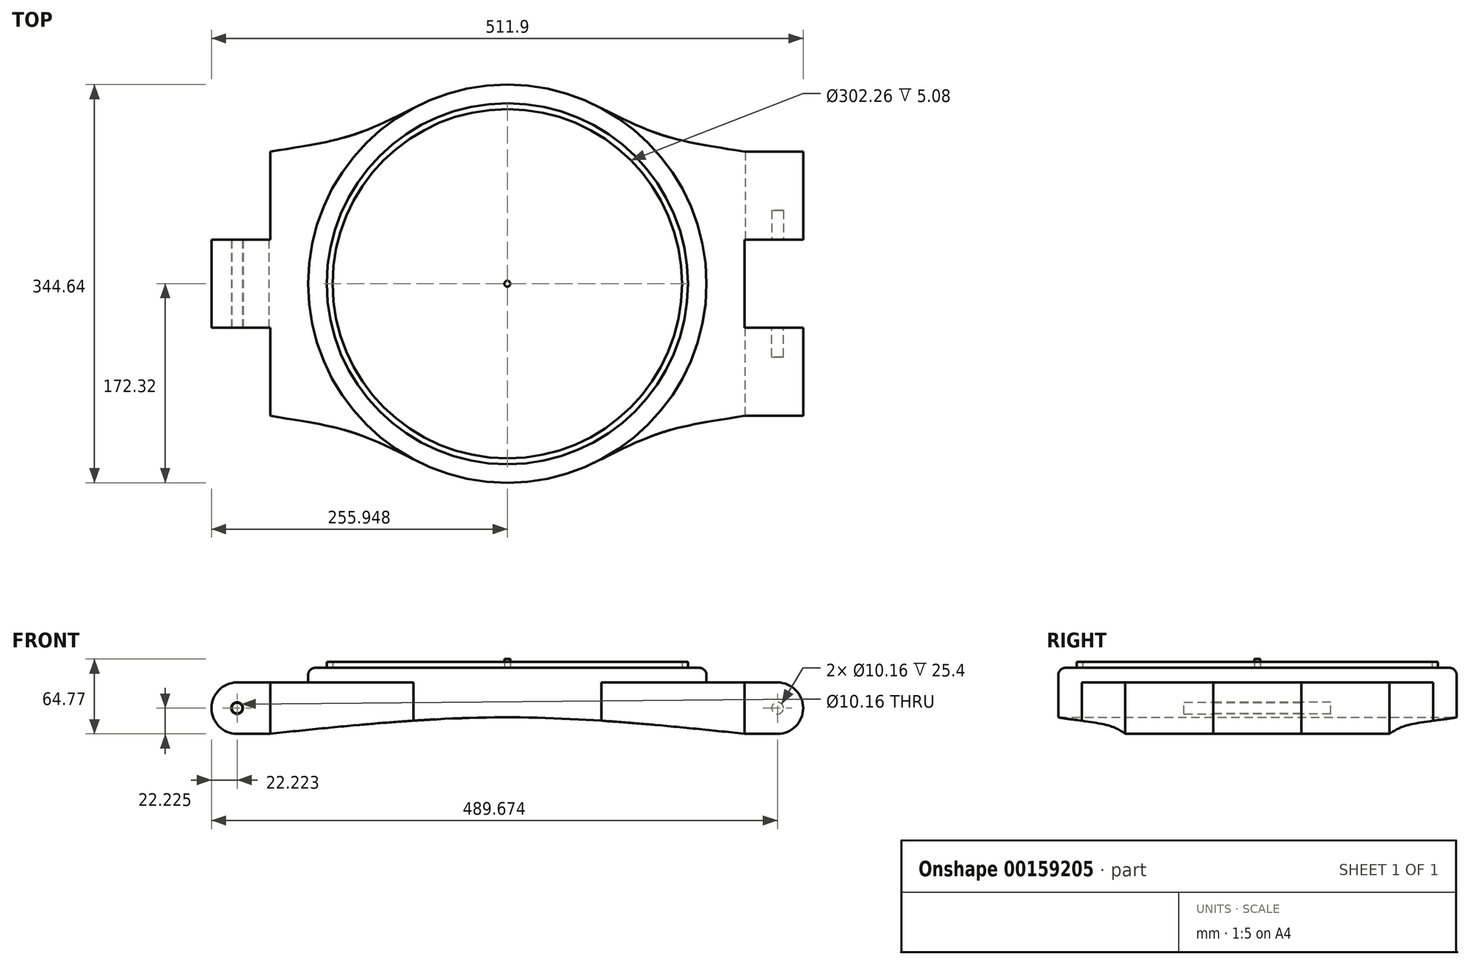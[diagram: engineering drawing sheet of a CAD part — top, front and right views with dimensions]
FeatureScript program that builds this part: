
annotation { "Feature Type Name" : "Feature", "Feature Type Description" : "" }
export const myFeature = defineFeature(function(context is Context, id is Id, definition is map)
    precondition{}
    {
        {
            var Q0;
            Q0=qCreatedBy(makeId("Top.planeOp"),FACE);
            var sketch = newSketch(context, id + "F0", { "sketchPlane" : qUnion([Q0])});
            skLineSegment(sketch, "E0", {"start": v(-15.4, -76.2) * mm, "end": v(-91.6, -76.2) * mm});
            skLineSegment(sketch, "E1", {"start": v(-91.6, -76.2) * mm, "end": v(-91.6, 0) * mm});
            skLineSegment(sketch, "E2", {"start": v(-91.6, 0) * mm, "end": v(-142.4, 0) * mm});
            skLineSegment(sketch, "E3", {"start": v(-142.4, 0) * mm, "end": v(-142.4, 76.2) * mm});
            skLineSegment(sketch, "E4", {"start": v(-142.4, 76.2) * mm, "end": v(-91.6, 76.2) * mm});
            skLineSegment(sketch, "E5", {"start": v(-91.6, 76.2) * mm, "end": v(-91.6, 152.4) * mm});
            skLineSegment(sketch, "E6", {"start": v(-91.6, 152.4) * mm, "end": v(-15.4, 152.4) * mm});
            skLineSegment(sketch, "E7", {"start": v(-15.4, 152.4) * mm, "end": v(-15.4, -76.2) * mm});
            skCircle(sketch, "E8", {"center": v(113.55, 38.1) * mm, "radius": 172.32 * mm});
            skPoint(sketch, "E8.centerSnap0", {"position": v(-15.4, 38.1) * mm});
            skLineSegment(sketch, "E9", {"start": v(242.5, 152.4) * mm, "end": v(242.5, -76.2) * mm});
            skLineSegment(sketch, "E10", {"start": v(242.5, -76.2) * mm, "end": v(369.5, -76.2) * mm});
            skLineSegment(sketch, "E11", {"start": v(369.5, -76.2) * mm, "end": v(369.5, 0) * mm});
            skLineSegment(sketch, "E12", {"start": v(369.5, 0) * mm, "end": v(318.7, 0) * mm});
            skLineSegment(sketch, "E13", {"start": v(318.7, 0) * mm, "end": v(318.7, 76.2) * mm});
            skLineSegment(sketch, "E14", {"start": v(318.7, 76.2) * mm, "end": v(369.5, 76.2) * mm});
            skLineSegment(sketch, "E15", {"start": v(369.5, 76.2) * mm, "end": v(369.5, 152.4) * mm});
            skLineSegment(sketch, "E16", {"start": v(369.5, 152.4) * mm, "end": v(242.5, 152.4) * mm});
            skFitSpline(sketch, "E17", {"points": [v(-91.6, -76.2) * mm, v(32.25, -113.83) * mm], "startDerivative": vector(178.39, -29.4) * mm, "endDerivative": vector(159.39, -81.53) * mm});
            skFitSpline(sketch, "E18.MirrorCS", {"points": [v(318.7, -76.2) * mm, v(194.84, -113.83) * mm], "startDerivative": vector(-178.39, -29.4) * mm, "endDerivative": vector(-159.39, -81.53) * mm});
            skFitSpline(sketch, "E19.MirrorCS", {"points": [v(318.7, 152.4) * mm, v(194.84, 190.03) * mm], "startDerivative": vector(-178.39, 29.4) * mm, "endDerivative": vector(-159.39, 81.53) * mm});
            skFitSpline(sketch, "E20.MirrorCS", {"points": [v(-91.6, 152.4) * mm, v(32.25, 190.03) * mm], "startDerivative": vector(178.39, 29.4) * mm, "endDerivative": vector(159.39, 81.53) * mm});
            skSolve(sketch);
        }
        {
            var Q0;
            {var subQ1=sQuery(id+"F0.wireOp",EDGE,"E7");Q0=makeQuery(id+"F0.imprint","IMPRINT",FACE,{"disambiguationData":[TD([[makeQuery(id+"F0.imprint","IMPRINT",EDGE,{"derivedFrom":subQ1}),1.0]])]});}
            var Q1;
            {var subQ0=sQuery(id+"F0.wireOp",EDGE,"E6");Q1=makeQuery(id+"F0.imprint","IMPRINT",FACE,{"disambiguationData":[TD([[makeQuery(id+"F0.imprint","IMPRINT",EDGE,{"derivedFrom":subQ0}),1.0]])]});}
            var Q2;
            {var subQ0=sQuery(id+"F0.wireOp",EDGE,"E0");Q2=makeQuery(id+"F0.imprint","IMPRINT",FACE,{"disambiguationData":[TD([[makeQuery(id+"F0.imprint","IMPRINT",EDGE,{"derivedFrom":subQ0}),-1.0]])]});}
            var Q3;
            {var subQ0=sQuery(id+"F0.wireOp",EDGE,"E0");Q3=makeQuery(id+"F0.imprint","IMPRINT",FACE,{"disambiguationData":[TD([[makeQuery(id+"F0.imprint","IMPRINT",EDGE,{"derivedFrom":subQ0}),1.0]])]});}
            var Q4;
            {var subQ0=sQuery(id+"F0.wireOp",EDGE,"E7");Q4=makeQuery(id+"F0.imprint","IMPRINT",FACE,{"disambiguationData":[TD([[makeQuery(id+"F0.imprint","IMPRINT",EDGE,{"derivedFrom":subQ0}),-1.0]])]});}
            var Q5;
            {var subQ0=sQuery(id+"F0.wireOp",EDGE,"E9");Q5=makeQuery(id+"F0.imprint","IMPRINT",FACE,{"disambiguationData":[TD([[makeQuery(id+"F0.imprint","IMPRINT",EDGE,{"derivedFrom":subQ0}),1.0]])]});}
            var Q6;
            {var subQ3=sQuery(id+"F0.wireOp",EDGE,"E18.MirrorCS");Q6=makeQuery(id+"F0.imprint","IMPRINT",FACE,{"disambiguationData":[TD([[makeQuery(id+"F0.imprint","IMPRINT",EDGE,{"derivedFrom":subQ3}),-1.0]])]});}
            var Q7;
            {var subQ0=sQuery(id+"F0.wireOp",EDGE,"E11");Q7=makeQuery(id+"F0.imprint","IMPRINT",FACE,{"disambiguationData":[TD([[makeQuery(id+"F0.imprint","IMPRINT",EDGE,{"derivedFrom":subQ0}),1.0]])]});}
            var Q8;
            {var subQ3=sQuery(id+"F0.wireOp",EDGE,"E19.MirrorCS");Q8=makeQuery(id+"F0.imprint","IMPRINT",FACE,{"disambiguationData":[TD([[makeQuery(id+"F0.imprint","IMPRINT",EDGE,{"derivedFrom":subQ3}),1.0]])]});}
            extrude(context, id + "F1", {"entities" : qUnion([Q0, Q1, Q2, Q3, Q4, Q5, Q6, Q7, Q8]), "oppositeDirection" : true, "depth" : 44.45 * mm});
        }
        {
            var Q0;
            Q0=makeQuery(id+"F1.opExtrude","CAP_EDGE",EDGE,{"disambiguationData":[OSD([sQuery(id+"F0.wireOp",EDGE,"E3")])],"isStart":true});
            var Q1;
            Q1=makeQuery(id+"F1.opExtrude","CAP_EDGE",EDGE,{"disambiguationData":[OSD([sQuery(id+"F0.wireOp",EDGE,"E3")])],"isStart":false});
            var Q2;
            Q2=makeQuery(id+"F1.opExtrude","CAP_EDGE",EDGE,{"disambiguationData":[OSD([sQuery(id+"F0.wireOp",EDGE,"E11")])],"isStart":true});
            var Q3;
            Q3=makeQuery(id+"F1.opExtrude","CAP_EDGE",EDGE,{"disambiguationData":[OSD([sQuery(id+"F0.wireOp",EDGE,"E15")])],"isStart":true});
            var Q4;
            Q4=makeQuery(id+"F1.opExtrude","CAP_EDGE",EDGE,{"disambiguationData":[OSD([sQuery(id+"F0.wireOp",EDGE,"E15")])],"isStart":false});
            var Q5;
            Q5=makeQuery(id+"F1.opExtrude","CAP_EDGE",EDGE,{"disambiguationData":[OSD([sQuery(id+"F0.wireOp",EDGE,"E11")])],"isStart":false});
            fillet(context, id + "F2", {"entities" : qUnion([Q0, Q1, Q2, Q3, Q4, Q5]), "radius" : 22.22 * mm, "tangentPropagation" : true, "allowEdgeOverflow" : false});
        }
        {
            var Q0;
            {var subQ1=sQuery(id+"F0.wireOp",EDGE,"E7");Q0=makeQuery(id+"F0.imprint","IMPRINT",FACE,{"disambiguationData":[TD([[makeQuery(id+"F0.imprint","IMPRINT",EDGE,{"derivedFrom":subQ1}),1.0]])]});}
            var Q1;
            {var subQ0=sQuery(id+"F0.wireOp",EDGE,"E7");Q1=makeQuery(id+"F0.imprint","IMPRINT",FACE,{"disambiguationData":[TD([[makeQuery(id+"F0.imprint","IMPRINT",EDGE,{"derivedFrom":subQ0}),-1.0]])]});}
            var Q2;
            {var subQ0=sQuery(id+"F0.wireOp",EDGE,"E9");Q2=makeQuery(id+"F0.imprint","IMPRINT",FACE,{"disambiguationData":[TD([[makeQuery(id+"F0.imprint","IMPRINT",EDGE,{"derivedFrom":subQ0}),1.0]])]});}
            extrude(context, id + "F3", {"entities" : qUnion([Q0, Q1, Q2]), "operationType" : NewBodyOperationType.ADD, "depth" : 12.7 * mm});
        }
        {
            var Q0;
            Q0=qCreatedBy(makeId("Front.planeOp"),FACE);
            var sketch = newSketch(context, id + "F4", { "sketchPlane" : qUnion([Q0])});
            skFitSpline(sketch, "E21", {"points": [v(-92.66, -44.45) * mm, v(113.22, -30.2) * mm, v(319.28, -44.45) * mm], "startDerivative": vector(411.8, 42.76) * mm, "endDerivative": vector(412.09, -42.76) * mm});
            skLineSegment(sketch, "E22", {"start": v(-92.66, -44.45) * mm, "end": v(319.28, -44.45) * mm});
            skSolve(sketch);
        }
        {
            var Q0;
            Q0 = qSketchRegion(id + "F4", true);
            extrude(context, id + "F5", {"entities" : qUnion([Q0]), "operationType" : NewBodyOperationType.REMOVE, "endBound" : BoundingType.THROUGH_ALL, "oppositeDirection" : true, "depth" : 254 * mm});
        }
        {
            var Q0;
            Q0 = qSketchRegion(id + "F4", true);
            extrude(context, id + "F6", {"entities" : qUnion([Q0]), "operationType" : NewBodyOperationType.REMOVE, "endBound" : BoundingType.THROUGH_ALL, "depth" : 25.4 * mm});
        }
        {
            var Q0;
            Q0=qCreatedBy(makeId("Front.planeOp"),FACE);
            var sketch = newSketch(context, id + "F7", { "sketchPlane" : qUnion([Q0])});
            skCircle(sketch, "E23", {"center": v(-120.18, -22.23) * mm, "radius": 5.08 * mm});
            skCircle(sketch, "E24", {"center": v(-120.18, -22.23) * mm, "radius": 4.6 * mm});
            skCircle(sketch, "E25", {"center": v(347.27, -22.23) * mm, "radius": 5.08 * mm});
            skSolve(sketch);
        }
        {
            var Q0;
            Q0 = qSketchRegion(id + "F7", true);
            extrude(context, id + "F8", {"entities" : qUnion([Q0]), "operationType" : NewBodyOperationType.REMOVE, "oppositeDirection" : true, "depth" : 101.6 * mm});
        }
        {
            var Q0;
            Q0 = qSketchRegion(id + "F7", true);
            extrude(context, id + "F9", {"entities" : qUnion([Q0]), "operationType" : NewBodyOperationType.REMOVE, "depth" : 25.4 * mm});
        }
        {
            var Q0;
            Q0=makeQuery(id+"F3.opExtrude","CAP_EDGE",EDGE,{"disambiguationData":[OSD([sQuery(id+"F0.wireOp",EDGE,"E8")])],"isStart":false});
            fillet(context, id + "F10", {"entities" : qUnion([Q0]), "radius" : 6.35 * mm, "tangentPropagation" : true, "allowEdgeOverflow" : false});
        }
        {
            var Q0;
            Q0=qCreatedBy(makeId("Top.planeOp"),FACE);
            var sketch = newSketch(context, id + "F11", { "sketchPlane" : qUnion([Q0])});
            skCircle(sketch, "E26", {"center": v(113.55, 38.1) * mm, "radius": 156.21 * mm});
            skCircle(sketch, "E27", {"center": v(113.55, 38.1) * mm, "radius": 151.13 * mm});
            skSolve(sketch);
        }
        {
            var Q0;
            Q0 = qSketchRegion(id + "F11", true);
            extrude(context, id + "F12", {"entities" : qUnion([Q0]), "operationType" : NewBodyOperationType.ADD, "depth" : 17.78 * mm});
        }
        {
            var Q0;
            Q0=qCreatedBy(makeId("Top.planeOp"),FACE);
            var sketch = newSketch(context, id + "F13", { "sketchPlane" : qUnion([Q0])});
            skCircle(sketch, "E28", {"center": v(113.55, 38.1) * mm, "radius": 2.54 * mm});
            skSolve(sketch);
        }
        {
            var Q0;
            Q0 = qSketchRegion(id + "F13", true);
            extrude(context, id + "F14", {"entities" : qUnion([Q0]), "operationType" : NewBodyOperationType.ADD, "depth" : 20.32 * mm});
        }
    });
